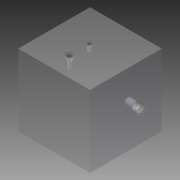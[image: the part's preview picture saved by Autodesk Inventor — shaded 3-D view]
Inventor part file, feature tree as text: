
AUTODESK INVENTOR PART (.ipt)
format: ipt  version: 2014 (Build 180170000, 170)  size: 256,512 bytes
history: native  units: mm
features: other x52, sketch x7, extrude x1
ambient origin geometry x8: Origin, YZ Plane, XZ Plane, XY Plane, X Axis, Y Axis, Z Axis, Center Point
bodies: 实体1 (feature_tree)
feature tree (60):
  other  "NULLNET"
  extrude  "拉伸1"  TaperAngle=0.0deg  [1 undecoded]
  other  "UCS1"
  other  "UCS2"
  other  "UCS3"
  other  "UCS4"
  other  "UCS5"
  other  "UCS6"
  sketch  "草图1"  dims[d0=300.0mm d1=0.0mm]
  sketch  "草图3"  dims[d8=0.0mm d9=0.0mm d10=0.0mm d11=0.0mm d12=0.0mm d13=0.0mm]
  other  "曲面1"
  sketch  "草图5"  dims[d20=0.0mm d21=0.0mm d22=0.0mm d23=0.0mm d24=0.0mm d25=0.0mm]
  other  "曲面2"
  sketch  "草图8"  dims[d32=0.0mm d33=0.0mm d34=0.0mm d35=0.0mm d36=0.0mm d37=0.0mm d38=0.0mm d42=-9.96mm d43=0.13mm d44=0.0mm d45=0.0mm d49=-19.0mm d50=0.13mm d51=0.0mm d55=0.0mm d59=-16.0mm d60=0.13mm d61=0.0mm]
  other  "曲面3"
  other  "UCS1: YZ 平面"
  other  "UCS1: XZ 平面"
  other  "UCS1: XY 平面"
  other  "UCS1: X 轴"
  other  "UCS1: Y 轴"
  other  "UCS1: Z 轴"
  other  "UCS1: 原点"
  other  "UCS2: YZ 平面"
  other  "UCS2: XZ 平面"
  other  "UCS2: XY 平面"
  other  "UCS2: X 轴"
  other  "UCS2: Y 轴"
  other  "UCS2: Z 轴"
  other  "UCS2: 原点"
  other  "UCS3: YZ 平面"
  other  "UCS3: XZ 平面"
  other  "UCS3: XY 平面"
  other  "UCS3: X 轴"
  other  "UCS3: Y 轴"
  other  "UCS3: Z 轴"
  other  "UCS3: 原点"
  other  "UCS4: YZ 平面"
  other  "UCS4: XZ 平面"
  other  "UCS4: XY 平面"
  other  "UCS4: X 轴"
  other  "UCS4: Y 轴"
  other  "UCS4: Z 轴"
  other  "UCS4: 原点"
  other  "UCS5: YZ 平面"
  other  "UCS5: XZ 平面"
  other  "UCS5: XY 平面"
  other  "UCS5: X 轴"
  other  "UCS5: Y 轴"
  other  "UCS5: Z 轴"
  other  "UCS5: 原点"
  other  "UCS6: YZ 平面"
  other  "UCS6: XZ 平面"
  other  "UCS6: XY 平面"
  other  "UCS6: X 轴"
  other  "UCS6: Y 轴"
  other  "UCS6: Z 轴"
  other  "UCS6: 原点"
  sketch  "草图2"  dims[d2=0.0mm d3=0.0mm d4=0.0mm d5=0.0mm d6=0.0mm d7=0.0mm]
  sketch  "草图4"  dims[d14=0.0mm d15=0.0mm d16=0.0mm d17=0.0mm d18=0.0mm d19=0.0mm]
  sketch  "草图7"  dims[d26=0.0mm d27=0.0mm d28=0.0mm d29=0.0mm d30=0.0mm d31=0.0mm]
note: 1 required parameter value undecoded (feature->parameter linkage not recoverable at this tier; creation-order binding heuristic only, values carry confidence <= 0.55)
